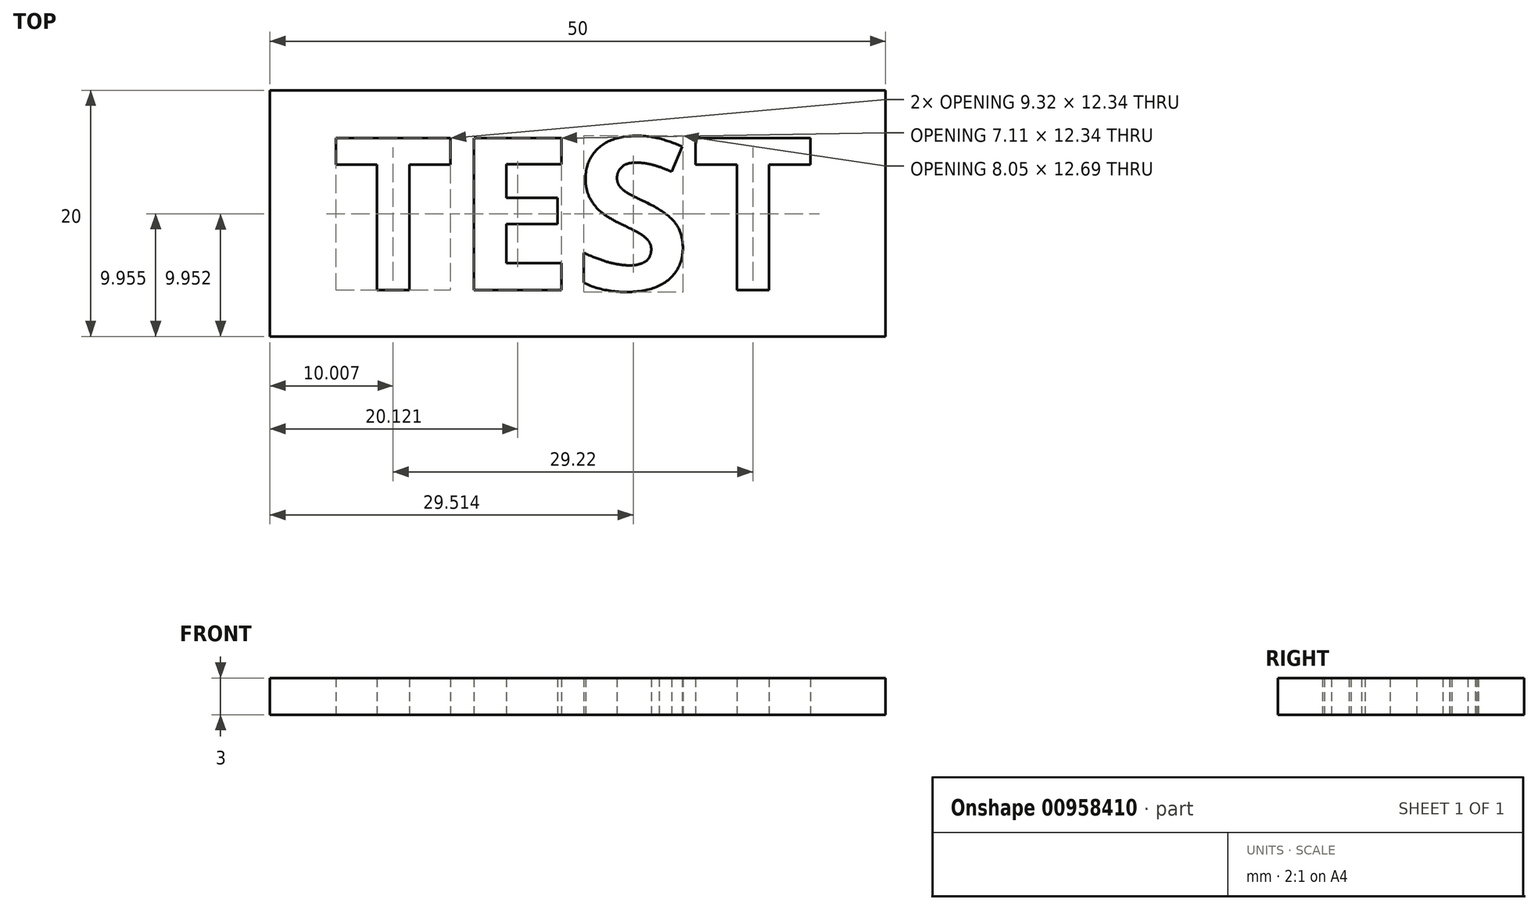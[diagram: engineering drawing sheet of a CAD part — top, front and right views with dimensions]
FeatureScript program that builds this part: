
annotation { "Feature Type Name" : "Feature", "Feature Type Description" : "" }
export const myFeature = defineFeature(function(context is Context, id is Id, definition is map)
    precondition{}
    {
        {
            var Q0;
            Q0=qCreatedBy(makeId("Top.planeOp"),FACE);
            var sketch = newSketch(context, id + "F0", { "sketchPlane" : qUnion([Q0])});
            skLineSegment(sketch, "E0.bottom", {"start": v(-25, 10) * mm, "end": v(25, 10) * mm});
            skLineSegment(sketch, "E0.top", {"start": v(-25, -10) * mm, "end": v(25, -10) * mm});
            skLineSegment(sketch, "E0.left", {"start": v(-25, 10) * mm, "end": v(-25, -10) * mm});
            skLineSegment(sketch, "E0.right", {"start": v(25, 10) * mm, "end": v(25, -10) * mm});
            skText(sketch, "E1", { "text": "TEST", "fontName": "OpenSans-Bold.ttf"});
            const initialGuessF0  = {"E1": [-0.02, -0.00622, 1, 0, 0.01245]};
            skSetInitialGuess(sketch, initialGuessF0);
            skSolve(sketch);
        }
        {
            var Q0;
            Q0=makeQuery(id+"F0.imprint","IMPRINT",FACE,{"disambiguationData":[TD([[makeQuery(id+"F0.imprint","IMPRINT",EDGE,{"derivedFrom":sQuery(id+"F0.wireOp",EDGE,"E0.bottom")}),-1.0]])]});
            extrude(context, id + "F1", {"entities" : qUnion([Q0]), "depth" : 3 * mm, "offsetDistance" : 25 * mm});
        }
    });
